# Revit family: Towel_Ring-American_Standard-Aspirations-7061190_Series
name_source: partatom
category: Specialty Equipment
units: mm (PartAtom-declared; Revit-internal decimal feet)

## family parameters
Cut with Voids When Loaded = No
Host = Face
OmniClass Number = 23.40.20.21.27
OmniClass Title = Towel Bars
Part Type = Normal
Room Calculation Point = No
Round Connector Dimension = Use Diameter
Shared = Yes

## types (3) — shared parameters
Assembly Code = C1030220
Default Elevation = 24"
Description = Towel Ring
Height = 6 1/2"
Installation Type = Wall Mounted
Length = 6 7/8"
Manufacturer = American Standard
URL = http://www.americanstandard-us.com
Width = 3 3/4"

## per-type parameters (varying)
| type | Finish | Material |
| 7061190.002 | Metal-American Standard-002-Polished Chrome | Metal-American Standard-002-Polished Chrome |
| 7061190.295 | Metal-American Standard-295-Brushed Nickel | Metal-American Standard-295-Brushed Nickel |
| 7061190.243 | Metal-American Standard-243-Matte Black | Metal-American Standard-243-Matte Black |

note: column(s) folded — value = type name in every type: Model

## geometry (parser evidence)
native form markers: Sweep x3
no freeform markers — native parametric forms only
